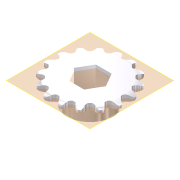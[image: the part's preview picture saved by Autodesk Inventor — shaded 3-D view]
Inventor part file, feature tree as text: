
AUTODESK INVENTOR PART (.ipt)
format: ipt  version: 2015 (Build 190159000, 159)  size: 519,168 bytes
history: native  units: mm
features: other x8, extrude x4, sketch x2, pattern_linear x1, pattern_circular x1
ambient origin geometry x8: Origin, YZ Plane, XZ Plane, XY Plane, X Axis, Y Axis, Z Axis, Center Point
bodies: Solid1 (feature_tree)
feature tree (16):
  other  "Blocks"
  other  "Theoretical Tooth Profile"
  other  "Tooth Profile"
  other  "Section Profile"
  other  "Shroud"
  other  "Strand"
  pattern_linear  "Strand Pattern"  Spacing1=1.6665mm  [1 undecoded]
  extrude  "Theoretical Tooth"  Depth=12.7mm
  extrude  "Tooth"  Depth=12.7mm
  pattern_circular  "Tooth Pattern"  [2 undecoded]
  other  "Timing Plane"
  extrude  "Extrusion4"  Depth=4.3065mm
  extrude  "Extrusion6"  Depth=12.7mm
  sketch  "Sketch4"  dims[d0=32.549026mm]
  other  "500Key"
  sketch  "Sketch6"  dims[d2=22.5deg d3=1.6665mm d10=22.471114mm d11=2.530727mm d12=2.64mm d13=4.3065mm d14=4.62mm d18=10.0mm d19=0.0mm d20=160.0mm d21=360.0deg d23=1.905mm d28=0.0mm d29=0.0mm d30=2.883mm d31=17.554806mm d32=2.883mm d33=0.8255mm d34=6.35mm d36=90.0deg d37=90.0deg d38=10.0mm d40=6.4mm d42=0.0mm d43=1.4415mm d44=23.452862mm d45=1.6665mm d46=7.128mm d47=0.0mm d48=25.4mm d49=0.0mm d50=10.0mm d51=21.59mm d52=7.493mm d53=0.0mm d54=12.7508mm d55=3.175mm d56=2.38125mm d59=12.7mm d60=25.4mm d61=0.0mm]
note: 3 required parameter values undecoded (feature->parameter linkage not recoverable at this tier; creation-order binding heuristic only, values carry confidence <= 0.55)
